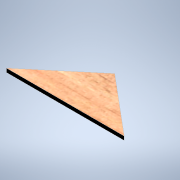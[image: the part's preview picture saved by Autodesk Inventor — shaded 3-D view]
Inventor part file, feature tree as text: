
AUTODESK INVENTOR PART (.ipt)
format: ipt  version: 2021 (Build 250183000, 183)  size: 112,128 bytes
history: native  units: mm
features: extrude x1, sketch x1
ambient origin geometry x8: Origin, YZ Plane, XZ Plane, XY Plane, X Axis, Y Axis, Z Axis, Center Point
bodies: Volumenkörper1 (feature_tree)
feature tree (2):
  extrude  "Extrusion1"  Depth=3.0mm TaperAngle=0.0deg
  sketch  "Skizze1"  dims[d0=93.0mm d2=3.0mm d3=0.0mm d4=39.0mm]
